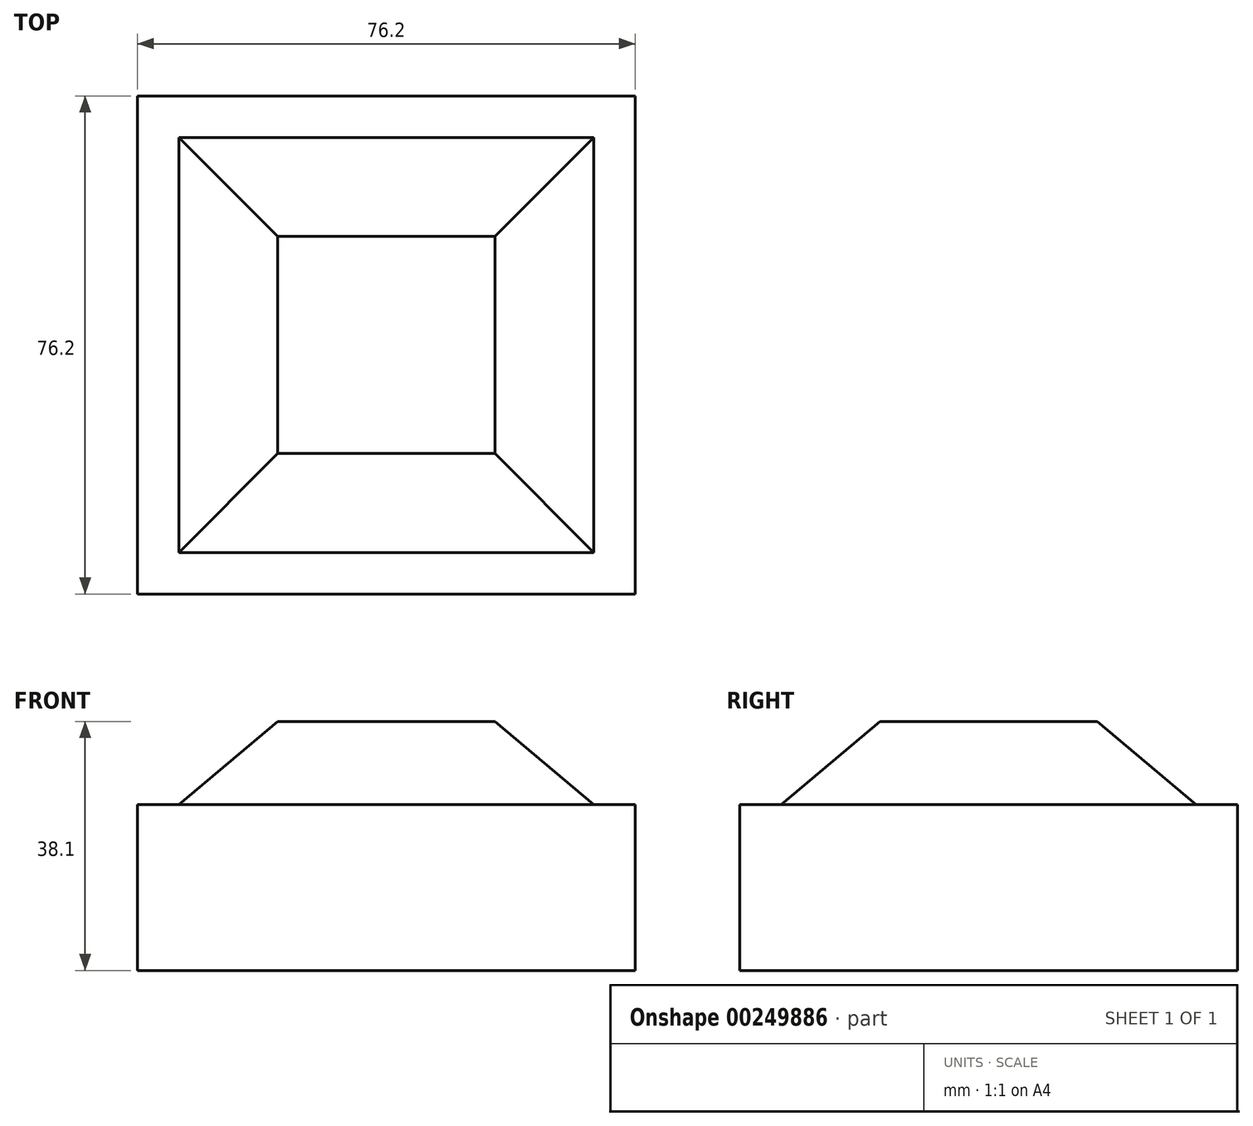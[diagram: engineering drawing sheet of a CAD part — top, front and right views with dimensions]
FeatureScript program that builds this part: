
annotation { "Feature Type Name" : "Feature", "Feature Type Description" : "" }
export const myFeature = defineFeature(function(context is Context, id is Id, definition is map)
    precondition{}
    {
        {
            var Q0;
            Q0=qCreatedBy(makeId("Top.planeOp"),FACE);
            var sketch = newSketch(context, id + "F0", { "sketchPlane" : qUnion([Q0])});
            skLineSegment(sketch, "E0.bottom", {"start": v(38.1, 38.1) * mm, "end": v(-38.1, 38.1) * mm});
            skLineSegment(sketch, "E0.top", {"start": v(38.1, -38.1) * mm, "end": v(-38.1, -38.1) * mm});
            skLineSegment(sketch, "E0.left", {"start": v(38.1, 38.1) * mm, "end": v(38.1, -38.1) * mm});
            skLineSegment(sketch, "E0.right", {"start": v(-38.1, 38.1) * mm, "end": v(-38.1, -38.1) * mm});
            skPoint(sketch, "E0.middle", {"position": v(0, 0) * mm});
            skSolve(sketch);
        }
        {
            var Q0;
            Q0 = qSketchRegion(id + "F0", true);
            extrude(context, id + "F1", {"entities" : qUnion([Q0]), "depth" : 25.4 * mm});
        }
        {
            var Q0;
            Q0=makeQuery(id+"F1.opExtrude","CAP_FACE",FACE,{"disambiguationData":[OSD([sQuery(id+"F0.wireOp",EDGE,"E0.bottom"),sQuery(id+"F0.wireOp",EDGE,"E0.top"),sQuery(id+"F0.wireOp",EDGE,"E0.left"),sQuery(id+"F0.wireOp",EDGE,"E0.right")])],"isStart":false});
            var sketch = newSketch(context, id + "F2", { "sketchPlane" : qUnion([Q0])});
            skLineSegment(sketch, "E1.bottom", {"start": v(31.75, 31.75) * mm, "end": v(-31.75, 31.75) * mm});
            skLineSegment(sketch, "E1.top", {"start": v(31.75, -31.75) * mm, "end": v(-31.75, -31.75) * mm});
            skLineSegment(sketch, "E1.left", {"start": v(31.75, 31.75) * mm, "end": v(31.75, -31.75) * mm});
            skLineSegment(sketch, "E1.right", {"start": v(-31.75, 31.75) * mm, "end": v(-31.75, -31.75) * mm});
            skPoint(sketch, "E1.middle", {"position": v(0, 0) * mm});
            skSolve(sketch);
        }
        {
            var Q0;
            Q0 = qSketchRegion(id + "F2", true);
            extrude(context, id + "F3", {"entities" : qUnion([Q0]), "operationType" : NewBodyOperationType.ADD, "depth" : 12.7 * mm});
        }
        {
            var Q0;
            Q0=makeQuery(id+"F3.opExtrude","CAP_EDGE",EDGE,{"disambiguationData":[OSD([sQuery(id+"F2.wireOp",EDGE,"E1.top")])],"isStart":false});
            var Q1;
            Q1=makeQuery(id+"F3.opExtrude","CAP_EDGE",EDGE,{"disambiguationData":[OSD([sQuery(id+"F2.wireOp",EDGE,"E1.right")])],"isStart":false});
            var Q2;
            Q2=makeQuery(id+"F3.opExtrude","CAP_EDGE",EDGE,{"disambiguationData":[OSD([sQuery(id+"F2.wireOp",EDGE,"E1.bottom")])],"isStart":false});
            var Q3;
            Q3=makeQuery(id+"F3.opExtrude","CAP_EDGE",EDGE,{"disambiguationData":[OSD([sQuery(id+"F2.wireOp",EDGE,"E1.left")])],"isStart":false});
            chamfer(context, id + "F4", {"entities" : qUnion([Q0, Q1, Q2, Q3]), "chamferType" : ChamferType.OFFSET_ANGLE, "width" : 12.7 * mm, "oppositeDirection" : false, "angle" : 50 * degree, "tangentPropagation" : true});
        }
    });
